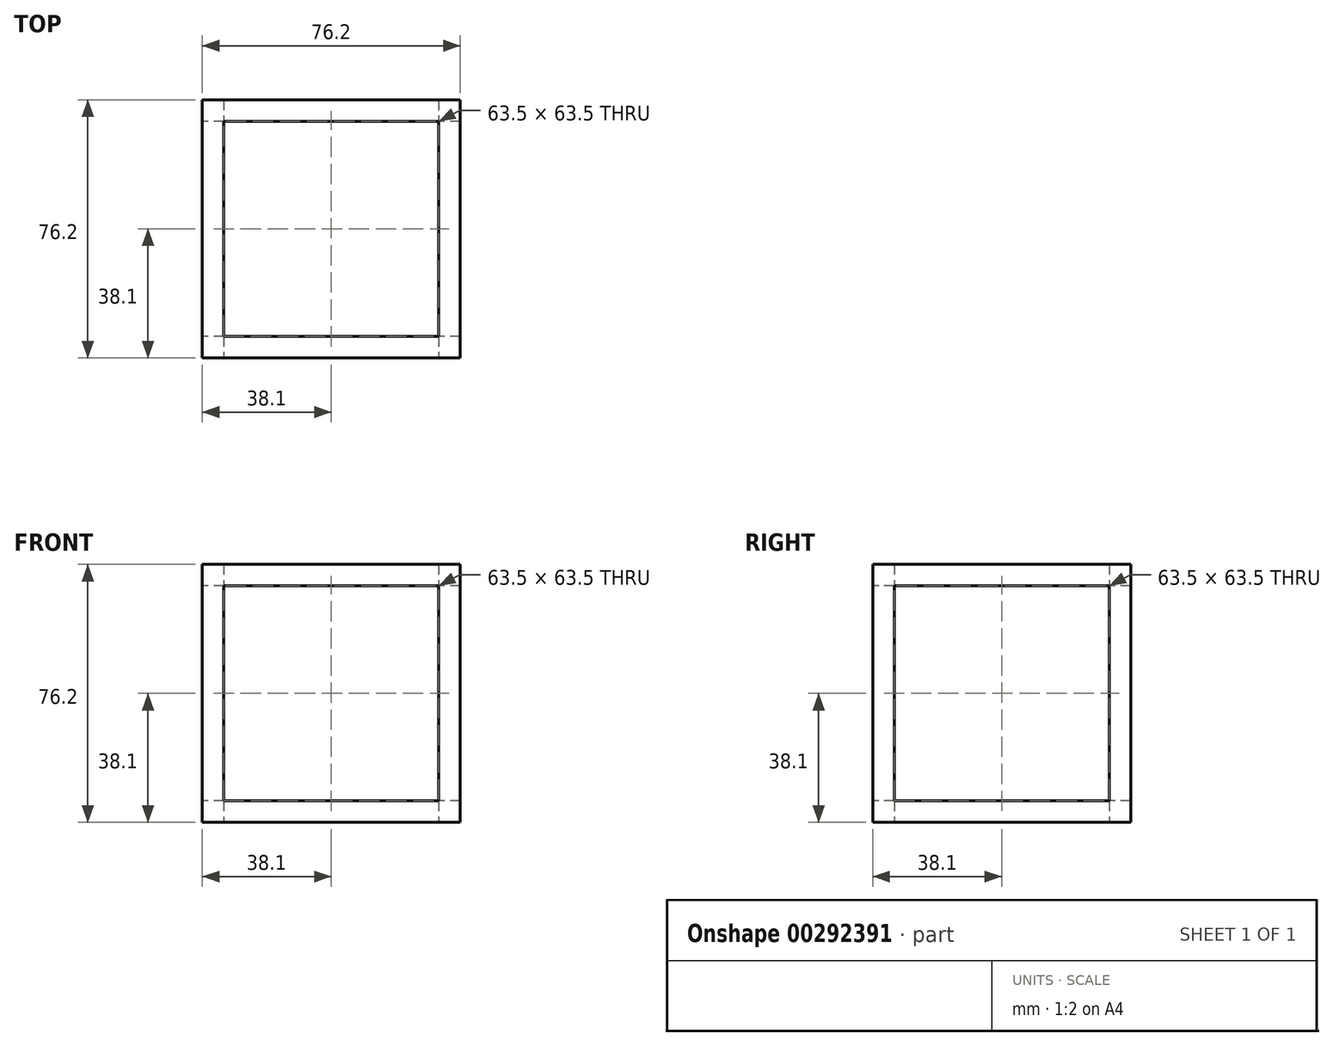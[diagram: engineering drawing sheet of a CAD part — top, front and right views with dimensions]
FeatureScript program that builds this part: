
annotation { "Feature Type Name" : "Feature", "Feature Type Description" : "" }
export const myFeature = defineFeature(function(context is Context, id is Id, definition is map)
    precondition{}
    {
        {
            var Q0;
            Q0=qCreatedBy(makeId("Top.planeOp"),FACE);
            var sketch = newSketch(context, id + "F0", { "sketchPlane" : qUnion([Q0])});
            skLineSegment(sketch, "E0.bottom", {"start": v(38.1, 38.1) * mm, "end": v(-38.1, 38.1) * mm});
            skLineSegment(sketch, "E0.top", {"start": v(38.1, -38.1) * mm, "end": v(-38.1, -38.1) * mm});
            skLineSegment(sketch, "E0.left", {"start": v(38.1, 38.1) * mm, "end": v(38.1, -38.1) * mm});
            skLineSegment(sketch, "E0.right", {"start": v(-38.1, 38.1) * mm, "end": v(-38.1, -38.1) * mm});
            skPoint(sketch, "E0.middle", {"position": v(0, 0) * mm});
            skSolve(sketch);
        }
        {
            var Q0;
            Q0=makeQuery(id+"F0.imprint","IMPRINT",FACE,{"disambiguationData":[TD([[makeQuery(id+"F0.imprint","IMPRINT",EDGE,{"derivedFrom":sQuery(id+"F0.wireOp",EDGE,"E0.bottom")}),1.0]])]});
            extrude(context, id + "F1", {"entities" : qUnion([Q0]), "depth" : 76.2 * mm});
        }
        {
            var Q0;
            Q0=makeQuery(id+"F1.opExtrude","SWEPT_FACE",FACE,{"disambiguationData":[OSD([sQuery(id+"F0.wireOp",EDGE,"E0.top")])]});
            var sketch = newSketch(context, id + "F2", { "sketchPlane" : qUnion([Q0])});
            skLineSegment(sketch, "E1.bottom", {"start": v(31.75, 69.85) * mm, "end": v(-31.75, 69.85) * mm});
            skLineSegment(sketch, "E1.top", {"start": v(31.75, 6.35) * mm, "end": v(-31.75, 6.35) * mm});
            skLineSegment(sketch, "E1.left", {"start": v(31.75, 69.85) * mm, "end": v(31.75, 6.35) * mm});
            skLineSegment(sketch, "E1.right", {"start": v(-31.75, 69.85) * mm, "end": v(-31.75, 6.35) * mm});
            skPoint(sketch, "E1.middle", {"position": v(0, 38.1) * mm});
            skSolve(sketch);
        }
        {
            var Q0;
            Q0=makeQuery(id+"F2.imprint","IMPRINT",FACE,{"disambiguationData":[TD([[makeQuery(id+"F2.imprint","IMPRINT",EDGE,{"derivedFrom":sQuery(id+"F2.wireOp",EDGE,"E1.bottom")}),1.0]])]});
            extrude(context, id + "F3", {"entities" : qUnion([Q0]), "operationType" : NewBodyOperationType.REMOVE, "oppositeDirection" : true, "depth" : 76.2 * mm});
        }
        {
            var Q0;
            Q0=makeQuery(id+"F1.opExtrude","SWEPT_FACE",FACE,{"disambiguationData":[OSD([sQuery(id+"F0.wireOp",EDGE,"E0.right")])]});
            var sketch = newSketch(context, id + "F4", { "sketchPlane" : qUnion([Q0])});
            skLineSegment(sketch, "E2.bottom", {"start": v(31.75, 69.85) * mm, "end": v(-31.75, 69.85) * mm});
            skLineSegment(sketch, "E2.top", {"start": v(31.75, 6.35) * mm, "end": v(-31.75, 6.35) * mm});
            skLineSegment(sketch, "E2.left", {"start": v(31.75, 69.85) * mm, "end": v(31.75, 6.35) * mm});
            skLineSegment(sketch, "E2.right", {"start": v(-31.75, 69.85) * mm, "end": v(-31.75, 6.35) * mm});
            skPoint(sketch, "E2.middle", {"position": v(0, 38.1) * mm});
            skSolve(sketch);
        }
        {
            var Q0;
            Q0=makeQuery(id+"F4.imprint","IMPRINT",FACE,{"disambiguationData":[TD([[makeQuery(id+"F4.imprint","IMPRINT",EDGE,{"derivedFrom":sQuery(id+"F4.wireOp",EDGE,"E2.bottom")}),1.0]])]});
            extrude(context, id + "F5", {"entities" : qUnion([Q0]), "operationType" : NewBodyOperationType.REMOVE, "oppositeDirection" : true, "depth" : 76.2 * mm});
        }
        {
            var Q0;
            Q0=makeQuery(id+"F1.opExtrude","CAP_FACE",FACE,{"disambiguationData":[OSD([sQuery(id+"F0.wireOp",EDGE,"E0.bottom"),sQuery(id+"F0.wireOp",EDGE,"E0.top"),sQuery(id+"F0.wireOp",EDGE,"E0.left"),sQuery(id+"F0.wireOp",EDGE,"E0.right")])],"isStart":true});
            var sketch = newSketch(context, id + "F6", { "sketchPlane" : qUnion([Q0])});
            skLineSegment(sketch, "E3.bottom", {"start": v(31.75, 31.75) * mm, "end": v(-31.75, 31.75) * mm});
            skLineSegment(sketch, "E3.top", {"start": v(31.75, -31.75) * mm, "end": v(-31.75, -31.75) * mm});
            skLineSegment(sketch, "E3.left", {"start": v(31.75, 31.75) * mm, "end": v(31.75, -31.75) * mm});
            skLineSegment(sketch, "E3.right", {"start": v(-31.75, 31.75) * mm, "end": v(-31.75, -31.75) * mm});
            skPoint(sketch, "E3.middle", {"position": v(0, 0) * mm});
            skSolve(sketch);
        }
        {
            var Q0;
            Q0=makeQuery(id+"F6.imprint","IMPRINT",FACE,{"disambiguationData":[TD([[makeQuery(id+"F6.imprint","IMPRINT",EDGE,{"derivedFrom":sQuery(id+"F6.wireOp",EDGE,"E3.bottom")}),1.0]])]});
            extrude(context, id + "F7", {"entities" : qUnion([Q0]), "operationType" : NewBodyOperationType.REMOVE, "oppositeDirection" : true, "depth" : 76.2 * mm});
        }
    });
